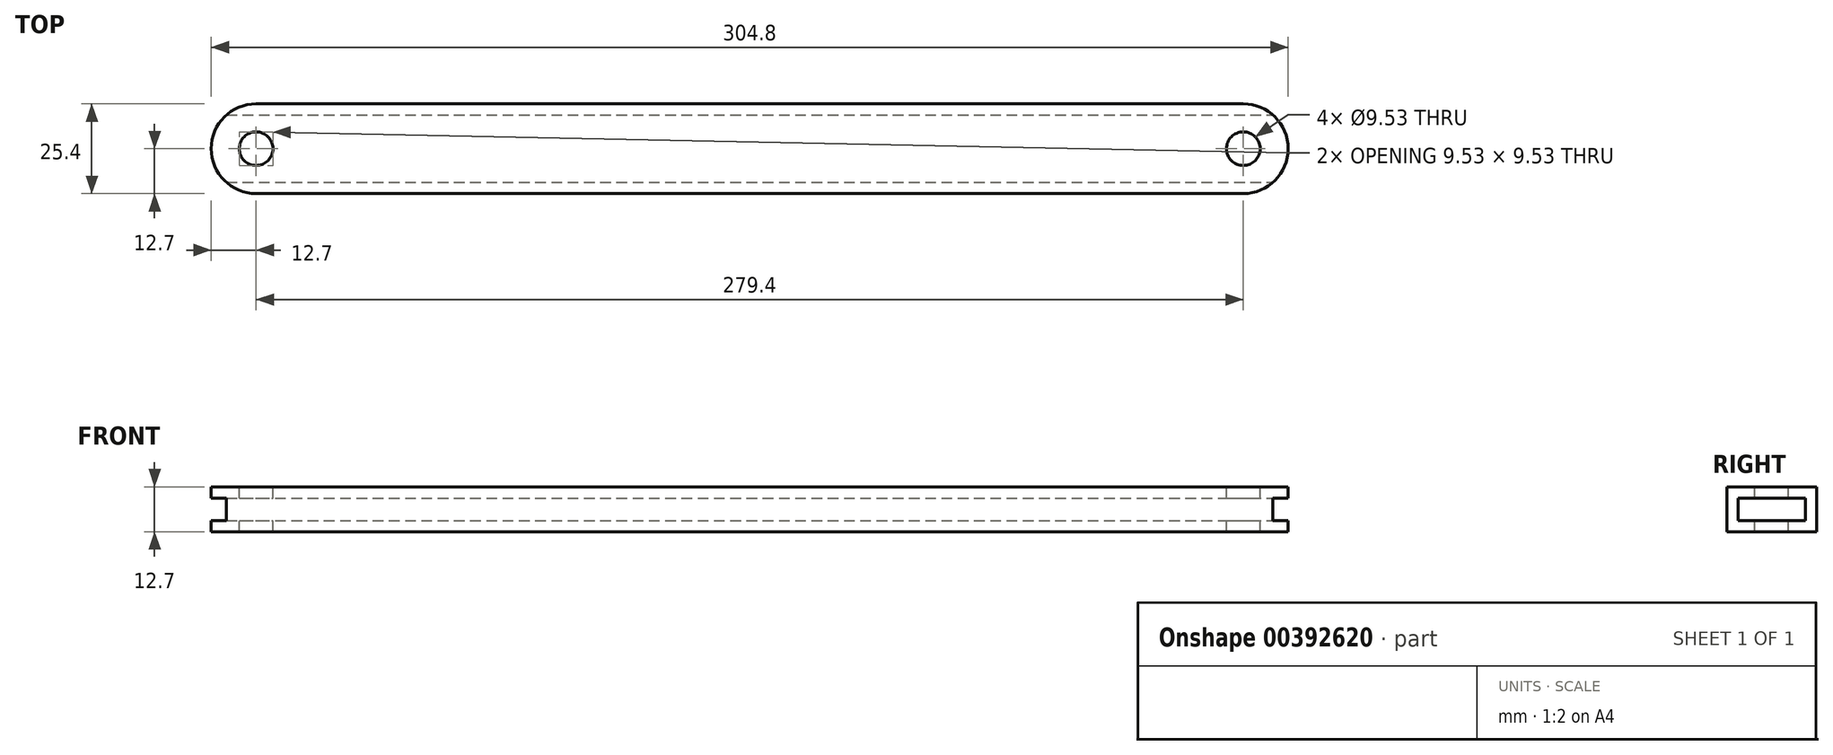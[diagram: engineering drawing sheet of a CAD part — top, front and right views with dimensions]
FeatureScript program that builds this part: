
annotation { "Feature Type Name" : "Feature", "Feature Type Description" : "" }
export const myFeature = defineFeature(function(context is Context, id is Id, definition is map)
    precondition{}
    {
        {
            var Q0;
            Q0=qCreatedBy(makeId("Top.planeOp"),FACE);
            var sketch = newSketch(context, id + "F0", { "sketchPlane" : qUnion([Q0])});
            skLineSegment(sketch, "E0.bottom", {"start": v(-152.4, 12.7) * mm, "end": v(152.4, 12.7) * mm});
            skLineSegment(sketch, "E0.top", {"start": v(-152.4, -12.7) * mm, "end": v(152.4, -12.7) * mm});
            skLineSegment(sketch, "E0.left", {"start": v(-152.4, 12.7) * mm, "end": v(-152.4, -12.7) * mm});
            skLineSegment(sketch, "E0.right", {"start": v(152.4, 12.7) * mm, "end": v(152.4, -12.7) * mm});
            skPoint(sketch, "E0.middle", {"position": v(0, 0) * mm});
            skSolve(sketch);
        }
        {
            var Q0;
            Q0 = qSketchRegion(id + "F0", true);
            extrude(context, id + "F1", {"entities" : qUnion([Q0]), "endBound" : BoundingType.SYMMETRIC, "depth" : 12.7 * mm});
        }
        {
            var Q0;
            Q0=makeQuery(id+"F1.opExtrude","SWEPT_EDGE",EDGE,{"disambiguationData":[OSD([sQuery(id+"F0.wireOp",EDGE,"E0.bottom"),sQuery(id+"F0.wireOp",EDGE,"E0.left")])]});
            var Q1;
            Q1=makeQuery(id+"F1.opExtrude","SWEPT_EDGE",EDGE,{"disambiguationData":[OSD([sQuery(id+"F0.wireOp",EDGE,"E0.top"),sQuery(id+"F0.wireOp",EDGE,"E0.left")])]});
            var Q2;
            Q2=makeQuery(id+"F1.opExtrude","SWEPT_EDGE",EDGE,{"disambiguationData":[OSD([sQuery(id+"F0.wireOp",EDGE,"E0.bottom"),sQuery(id+"F0.wireOp",EDGE,"E0.right")])]});
            var Q3;
            Q3=makeQuery(id+"F1.opExtrude","SWEPT_EDGE",EDGE,{"disambiguationData":[OSD([sQuery(id+"F0.wireOp",EDGE,"E0.top"),sQuery(id+"F0.wireOp",EDGE,"E0.right")])]});
            fillet(context, id + "F2", {"entities" : qUnion([Q0, Q1, Q2, Q3]), "radius" : 12.7 * mm, "tangentPropagation" : true, "allowEdgeOverflow" : false});
        }
        {
            var Q0;
            Q0=makeQuery(id+"F1.opExtrude","CAP_FACE",FACE,{"disambiguationData":[OSD([sQuery(id+"F0.wireOp",EDGE,"E0.bottom"),sQuery(id+"F0.wireOp",EDGE,"E0.top"),sQuery(id+"F0.wireOp",EDGE,"E0.left"),sQuery(id+"F0.wireOp",EDGE,"E0.right")])],"isStart":false});
            var sketch = newSketch(context, id + "F3", { "sketchPlane" : qUnion([Q0])});
            skCircle(sketch, "E1", {"center": v(-139.7, 0) * mm, "radius": 4.76 * mm});
            skCircle(sketch, "E2", {"center": v(139.7, 0) * mm, "radius": 4.76 * mm});
            skSolve(sketch);
        }
        {
            var Q0;
            Q0 = qSketchRegion(id + "F3", true);
            extrude(context, id + "F4", {"entities" : qUnion([Q0]), "operationType" : NewBodyOperationType.REMOVE, "endBound" : BoundingType.THROUGH_ALL, "oppositeDirection" : true, "depth" : 25.4 * mm});
        }
        {
            var Q0;
            Q0=qCreatedBy(makeId("Right.planeOp"),FACE);
            var sketch = newSketch(context, id + "F5", { "sketchPlane" : qUnion([Q0])});
            skLineSegment(sketch, "E3.bottom", {"start": v(-9.52, 3.18) * mm, "end": v(9.53, 3.18) * mm});
            skLineSegment(sketch, "E3.top", {"start": v(-9.53, -3.18) * mm, "end": v(9.53, -3.18) * mm});
            skLineSegment(sketch, "E3.left", {"start": v(-9.53, 3.18) * mm, "end": v(-9.53, -3.17) * mm});
            skLineSegment(sketch, "E3.right", {"start": v(9.53, 3.18) * mm, "end": v(9.53, -3.17) * mm});
            skPoint(sketch, "E3.middle", {"position": v(0, 0) * mm});
            skSolve(sketch);
        }
        {
            var Q0;
            Q0 = qSketchRegion(id + "F5", true);
            extrude(context, id + "F6", {"entities" : qUnion([Q0]), "operationType" : NewBodyOperationType.REMOVE, "endBound" : BoundingType.THROUGH_ALL, "oppositeDirection" : true, "depth" : 169.67 * mm, "hasSecondDirection" : true, "secondDirectionBound" : SecondDirectionBoundingType.THROUGH_ALL, "secondDirectionOppositeDirection" : false, "secondDirectionDepth" : 25.4 * mm});
        }
    });
